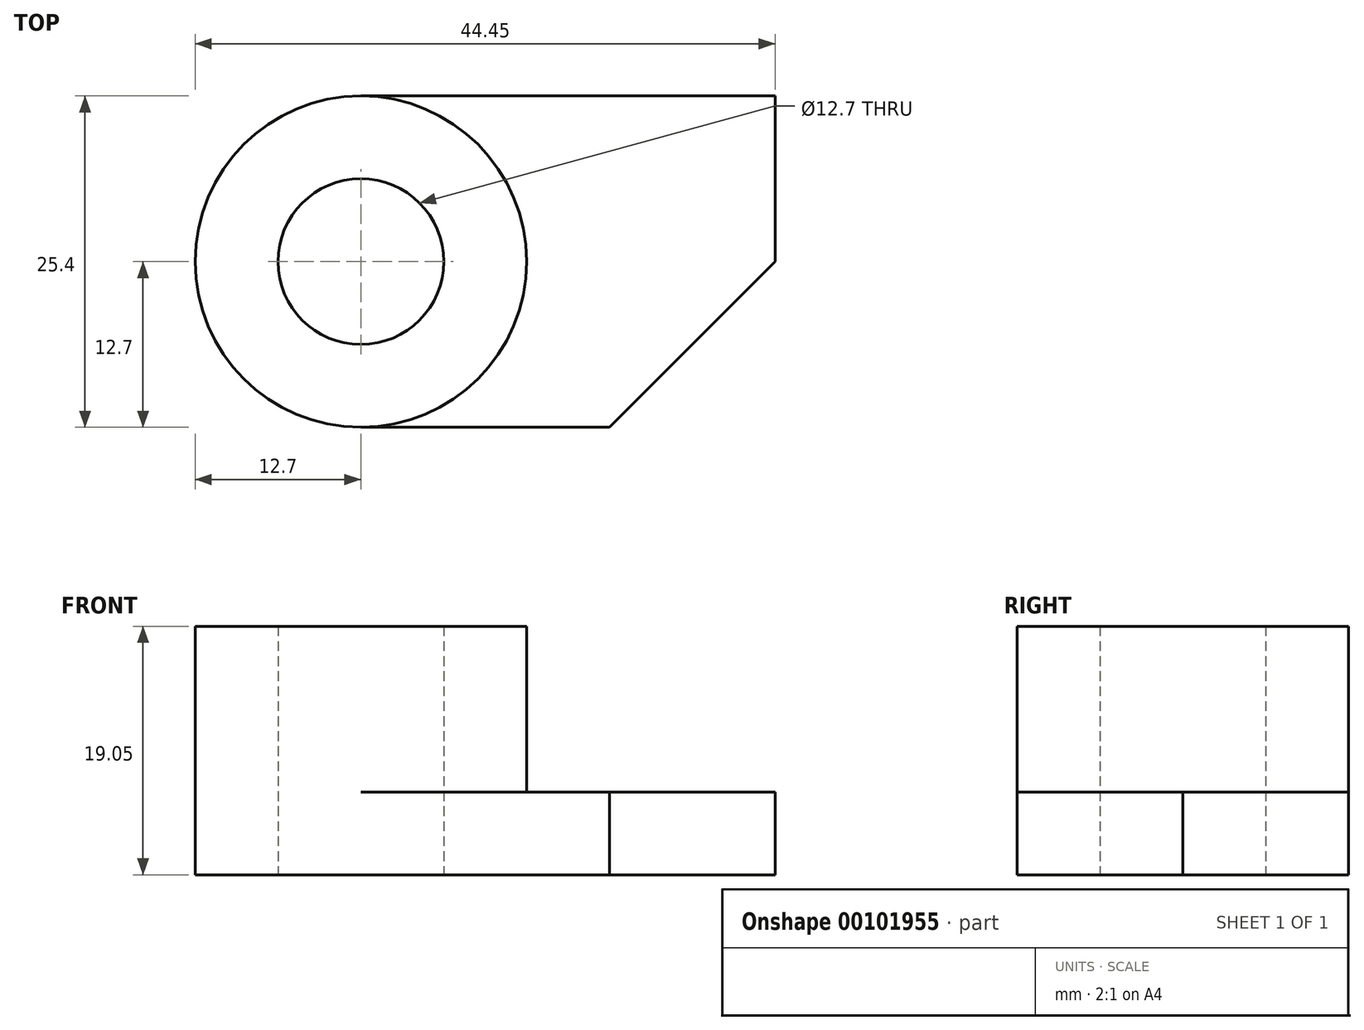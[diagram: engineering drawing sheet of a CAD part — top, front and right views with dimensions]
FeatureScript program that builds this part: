
annotation { "Feature Type Name" : "Feature", "Feature Type Description" : "" }
export const myFeature = defineFeature(function(context is Context, id is Id, definition is map)
    precondition{}
    {
        {
            var Q0;
            Q0=qCreatedBy(makeId("Top.planeOp"),FACE);
            var sketch = newSketch(context, id + "F0", { "sketchPlane" : qUnion([Q0])});
            skCircle(sketch, "E0", {"center": v(0, 0) * mm, "radius": 12.7 * mm});
            skCircle(sketch, "E1", {"center": v(0, 0) * mm, "radius": 6.35 * mm});
            skSolve(sketch);
        }
        {
            var Q0;
            Q0=makeQuery(id+"F0.imprint","IMPRINT",FACE,{"disambiguationData":[TD([[makeQuery(id+"F0.imprint","IMPRINT",EDGE,{"derivedFrom":sQuery(id+"F0.wireOp",EDGE,"E0")}),1.0]])]});
            extrude(context, id + "F1", {"entities" : qUnion([Q0]), "depth" : 19.05 * mm});
        }
        {
            var Q0;
            Q0=qCreatedBy(makeId("Top.planeOp"),FACE);
            var sketch = newSketch(context, id + "F2", { "sketchPlane" : qUnion([Q0])});
            skLineSegment(sketch, "E2", {"start": v(0, 12.7) * mm, "end": v(31.75, 12.7) * mm});
            skLineSegment(sketch, "E3", {"start": v(31.75, 12.7) * mm, "end": v(31.75, 0) * mm});
            skLineSegment(sketch, "E4", {"start": v(31.75, 0) * mm, "end": v(19.05, -12.7) * mm});
            skLineSegment(sketch, "E5", {"start": v(19.05, -12.7) * mm, "end": v(0, -12.7) * mm});
            skLineSegment(sketch, "E6", {"start": v(0, -12.7) * mm, "end": v(0, 12.7) * mm});
            skSolve(sketch);
        }
        {
            var Q0;
            Q0=makeQuery(id+"F2.imprint","IMPRINT",FACE,{"disambiguationData":[TD([[makeQuery(id+"F2.imprint","IMPRINT",EDGE,{"derivedFrom":sQuery(id+"F2.wireOp",EDGE,"E2")}),-1.0]])]});
            extrude(context, id + "F3", {"entities" : qUnion([Q0]), "operationType" : NewBodyOperationType.ADD, "depth" : 6.35 * mm});
        }
        {
            var Q0;
            Q0=makeQuery(id+"F1.opExtrude","CAP_FACE",FACE,{"disambiguationData":[OSD([sQuery(id+"F0.wireOp",EDGE,"E0"),sQuery(id+"F0.wireOp",EDGE,"E1")])],"isStart":false});
            var sketch = newSketch(context, id + "F4", { "sketchPlane" : qUnion([Q0])});
            skCircle(sketch, "E7", {"center": v(0, 0) * mm, "radius": 6.35 * mm});
            skSolve(sketch);
        }
        {
            var Q0;
            Q0=makeQuery(id+"F4.imprint","IMPRINT",FACE,{"disambiguationData":[TD([[makeQuery(id+"F4.imprint","IMPRINT",EDGE,{"derivedFrom":sQuery(id+"F4.wireOp",EDGE,"E7")}),1.0]])]});
            extrude(context, id + "F5", {"entities" : qUnion([Q0]), "operationType" : NewBodyOperationType.REMOVE, "oppositeDirection" : true, "depth" : 25.4 * mm});
        }
    });
